# Revit family: Basin-Sloan-SloanStone-ELRF_Series
name_source: partatom
category: Plumbing Fixtures
revit_build: Autodesk Revit 2014 (Build: 20130308_1515(x64)
units: mm (PartAtom-declared; Revit-internal decimal feet)

## types (4) — shared parameters
ADA Compliant = Yes
Assembly Code = D2010300
Basin Shape = Rectangular
CW Connection = Yes
CW Inlet Diameter = 0"
CWFU = 1.5
Cold Water Connection Diameter = 1/2"
Cold Water Connection Height = 24"
Cold Water Connection Radius = 1/4"
Cold Water Connection Width = 4"
Default Elevation = 34"
Description = SloanStone® Single Station Solid Surface lavatory.
Faucet Holes = Yes
Finish = SloanStone-Sloan-WH-White
HW Connection = Yes
HW Inlet Diameter = 0"
HWFU = 1.5
Height = 5"
Hot Water Connection Diameter = 1/2"
Hot Water Connection Height = 24"
Hot Water Connection Width = 4"
IAPMO Compliance = cUPC
Installation Type = Wall Mounted
Length = 24"
Manufacturer = SLOAN
Material = SloanStone-Sloan-WH-White
Price = Prices may vary. Please consult Manufacturer Representative for most up-to-date price list.
Product Documentation Link = https://specifications.sloan.com
Revised Date = 05/25/2018
Soap Dispenser Hole Punch = 0"
Soap Dispenser Holes = Yes
URL = https://www.sloan.com
Vent Connection = No
WFU = 2
Warranty Information = 3 Year Limited Warranty
Waste Connection = Yes
Waste Connection Description = 1-1/2'' Sanitary Outlet 2
Waste Connection Diameter = 1 1/2"
Waste Connection Height = 20"
Waste Connection Radius = 3/4"

## per-type parameters (varying)
| type | 4 CW Description | 4 CW Diameter | 4 HW Description | 4 HW Diameter | 4/2 CW Description | 4/2 HW Description | C CW Inlet Diameter | C HW Inlet Diameter | Center CW Connection Description | Center HW Connection Description | Center Hole Punch | Center Hole Punch Length | Faucet Hole Punch | Four Station Hole Length | Four Station Hole Punch | Graphics 1 | Outlet Description | Outlet Diameter | Waste Connection Width | Width |
| ELRF-81000 |  | 0" |  | 0" |  |  | 0" | 0" |  |  | No | 2 1/2" | 0" | 2 1/2" | No | No | 1-1/2'' Sanitary Outlet 1 | 1 1/2" | 0" | 30" |
| ELRF-82000 | 1/2'' CW Inlet 3 | 1/2" | 1/2'' HW Inlet 3 | 1/2" | 1/2'' CW Inlet 4 | 1/2'' HW Inlet 4 | 0" | 0" |  |  | No | 2 1/2" | 15" | 10" | Yes | Yes |  | 0" | 0" | 60" |
| ELRF-83000 |  | 0" |  | 0" |  |  | 1/2" | 1/2" | 1/2'' CW Inlet 5 | 1/2'' HW Inlet 5 | Yes | 10" | 30" | 2 1/2" | No | No | 1-1/2'' Sanitary Outlet 1 | 1 1/2" | 20 1/2" | 90" |
| ELRF-84000 | 1/2'' CW Inlet 3 | 1/2" | 1/2'' HW Inlet 3 | 1/2" | 1/2'' CW Inlet 4 | 1/2'' HW Inlet 4 | 0" | 0" |  |  | No | 2 1/2" | 45" | 10" | Yes | Yes |  | 0" | 27 1/8" | 120" |

note: column(s) folded — value = type name in every type: Model

## geometry (parser evidence)
native form markers: Sweep x3
no freeform markers — native parametric forms only
